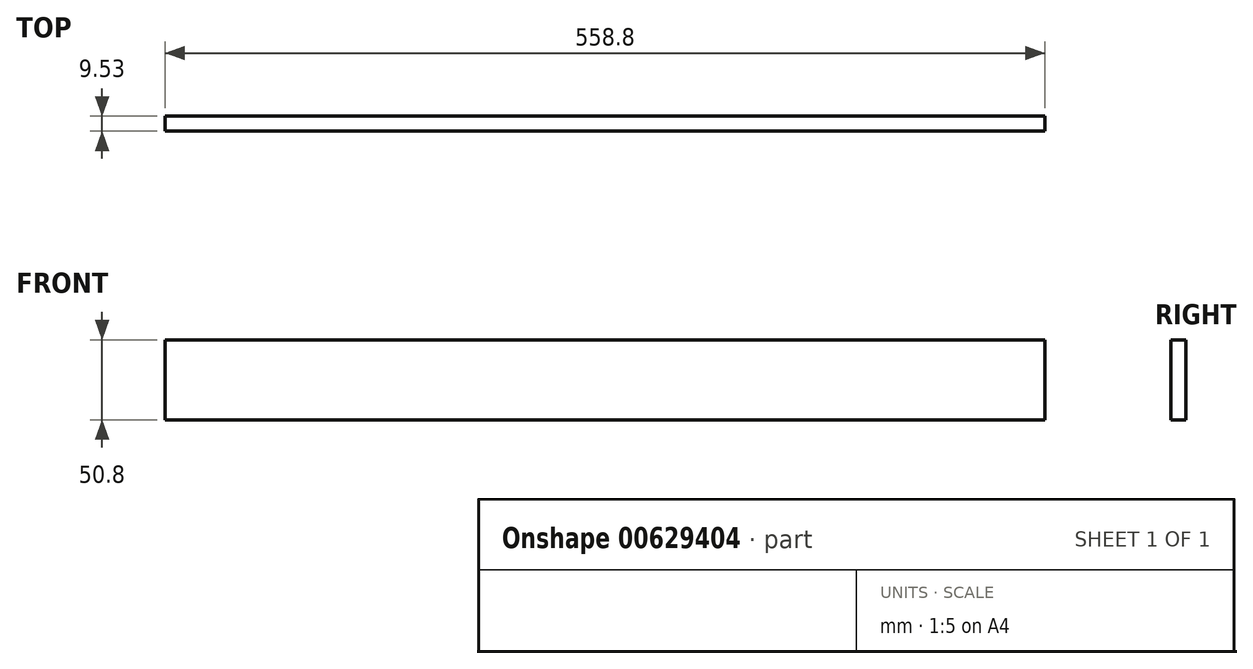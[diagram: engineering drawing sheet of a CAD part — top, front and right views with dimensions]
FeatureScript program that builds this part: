
annotation { "Feature Type Name" : "Feature", "Feature Type Description" : "" }
export const myFeature = defineFeature(function(context is Context, id is Id, definition is map)
    precondition{}
    {
        {
            var Q0;
            Q0=qCreatedBy(makeId("Front.planeOp"),FACE);
            var sketch = newSketch(context, id + "F0", { "sketchPlane" : qUnion([Q0])});
            skLineSegment(sketch, "E0.bottom", {"start": v(0, 0) * mm, "end": v(558.8, 0) * mm});
            skLineSegment(sketch, "E0.top", {"start": v(0, 50.8) * mm, "end": v(558.8, 50.8) * mm});
            skLineSegment(sketch, "E0.left", {"start": v(0, 0) * mm, "end": v(0, 50.8) * mm});
            skLineSegment(sketch, "E0.right", {"start": v(558.8, 0) * mm, "end": v(558.8, 50.8) * mm});
            skSolve(sketch);
        }
        {
            var Q0;
            Q0=qSketchRegion(id+"F0",true);
            extrude(context, id + "F1", {"entities" : qUnion([Q0]), "depth" : 9.52 * mm, "offsetDistance" : 25.4 * mm});
        }
    });
